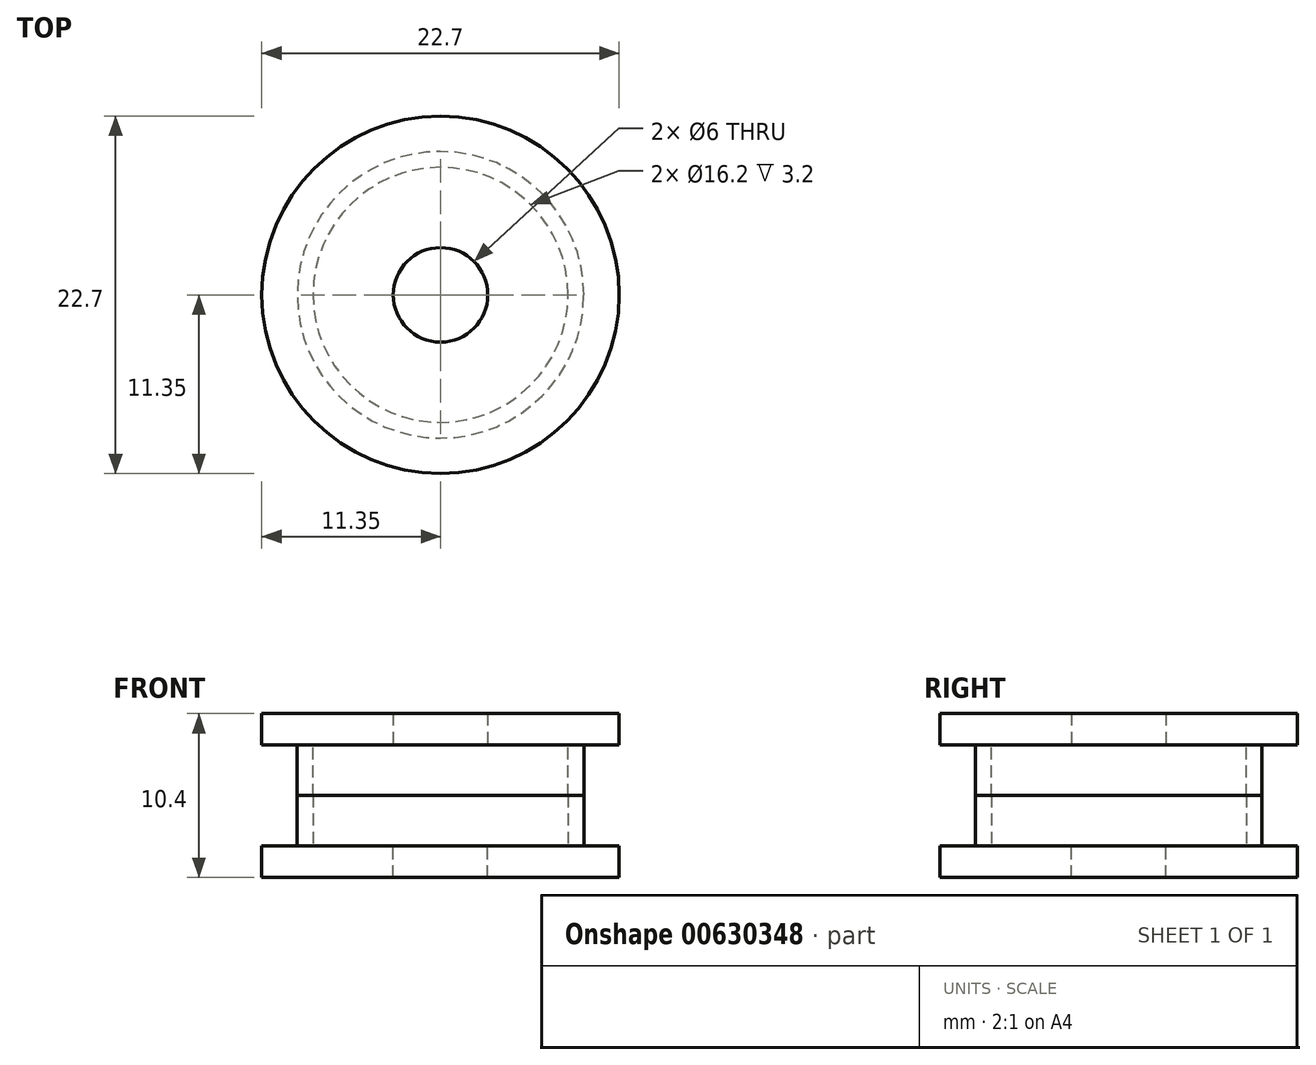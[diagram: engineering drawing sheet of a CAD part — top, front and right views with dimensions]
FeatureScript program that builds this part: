
annotation { "Feature Type Name" : "Feature", "Feature Type Description" : "" }
export const myFeature = defineFeature(function(context is Context, id is Id, definition is map)
    precondition{}
    {
        {
            var Q0;
            Q0=qCreatedBy(makeId("Top.planeOp"),FACE);
            var sketch = newSketch(context, id + "F0", { "sketchPlane" : qUnion([Q0])});
            skCircle(sketch, "E0", {"center": v(0, 0) * mm, "radius": 11.35 * mm});
            skCircle(sketch, "E1", {"center": v(0, 0) * mm, "radius": 9.1 * mm});
            skCircle(sketch, "E2", {"center": v(0, 0) * mm, "radius": 8.1 * mm});
            skCircle(sketch, "E3", {"center": v(0, 0) * mm, "radius": 3 * mm});
            skSolve(sketch);
        }
        {
            var Q0;
            Q0 = qSketchRegion(id + "F0", true);
            var Q1;
            Q1=makeQuery(id+"F0.imprint","IMPRINT",FACE,{"disambiguationData":[TD([[makeQuery(id+"F0.imprint","IMPRINT",EDGE,{"derivedFrom":sQuery(id+"F0.wireOp",EDGE,"E1")}),1.0]])]});
            var Q2;
            Q2=makeQuery(id+"F0.imprint","IMPRINT",FACE,{"disambiguationData":[TD([[makeQuery(id+"F0.imprint","IMPRINT",EDGE,{"derivedFrom":sQuery(id+"F0.wireOp",EDGE,"E2")}),1.0]])]});
            extrude(context, id + "F1", {"entities" : qUnion([Q0, Q1, Q2]), "oppositeDirection" : true, "depth" : 2 * mm, "offsetDistance" : 25 * mm});
        }
        {
            var Q0;
            Q0=makeQuery(id+"F0.imprint","IMPRINT",FACE,{"disambiguationData":[TD([[makeQuery(id+"F0.imprint","IMPRINT",EDGE,{"derivedFrom":sQuery(id+"F0.wireOp",EDGE,"E1")}),1.0]])]});
            extrude(context, id + "F2", {"entities" : qUnion([Q0]), "operationType" : NewBodyOperationType.ADD, "depth" : 3.2 * mm, "offsetDistance" : 25 * mm});
        }
        {
            var Q0;
            Q0=makeQuery(id+"F1.opExtrude","SWEPT_BODY",BODY,{"disambiguationData":[OSD([sQuery(id+"F0.wireOp",EDGE,"E0"),sQuery(id+"F0.wireOp",EDGE,"E3")])]});
            var Q1;
            Q1=makeQuery(id+"F2.opExtrude","CAP_FACE",FACE,{"disambiguationData":[OSD([sQuery(id+"F0.wireOp",EDGE,"E1"),sQuery(id+"F0.wireOp",EDGE,"E2")])],"isStart":false});
            mirror(context, id + "F3", {"entities" : qUnion([Q0]), "mirrorPlane" : qUnion([Q1])});
        }
    });
